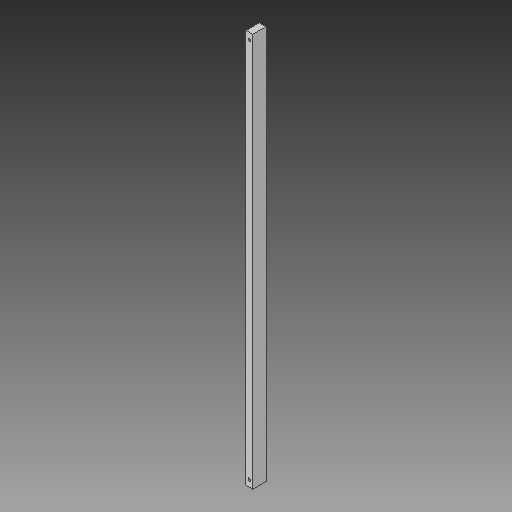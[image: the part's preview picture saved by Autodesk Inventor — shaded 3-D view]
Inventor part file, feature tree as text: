
AUTODESK INVENTOR PART (.ipt)
format: ipt  version: 2019 (Build 230136000, 136)  size: 110,592 bytes
history: native  units: in
note: dims shown in document units (in); Inventor stores cm internally (conversion verified against a paired STEP export)
features: sketch x2, extrude x1, hole x1
ambient origin geometry x8: Origin, YZ Plane, XZ Plane, XY Plane, X Axis, Y Axis, Z Axis, Center Point
bodies: Solid1 (feature_tree)
feature tree (4):
  extrude  "Extrusion1"  Depth=14.75in
  hole  "Hole1"  [1 undecoded]
  sketch  "Sketch1"  dims[d0=0.25in d1=14.75in]
  sketch  "Sketch2"  dims[d2=0.5in d3=0.0in d4=0.25in d5=0.14in d6=0.25in d7=0.14in d10=0.104in d11=0.5in d12=0.375in d13=0.25in d14=0.5635in d15=0.5in d16=0.8108in]
note: 1 required parameter value undecoded (feature->parameter linkage not recoverable at this tier; creation-order binding heuristic only, values carry confidence <= 0.55)
